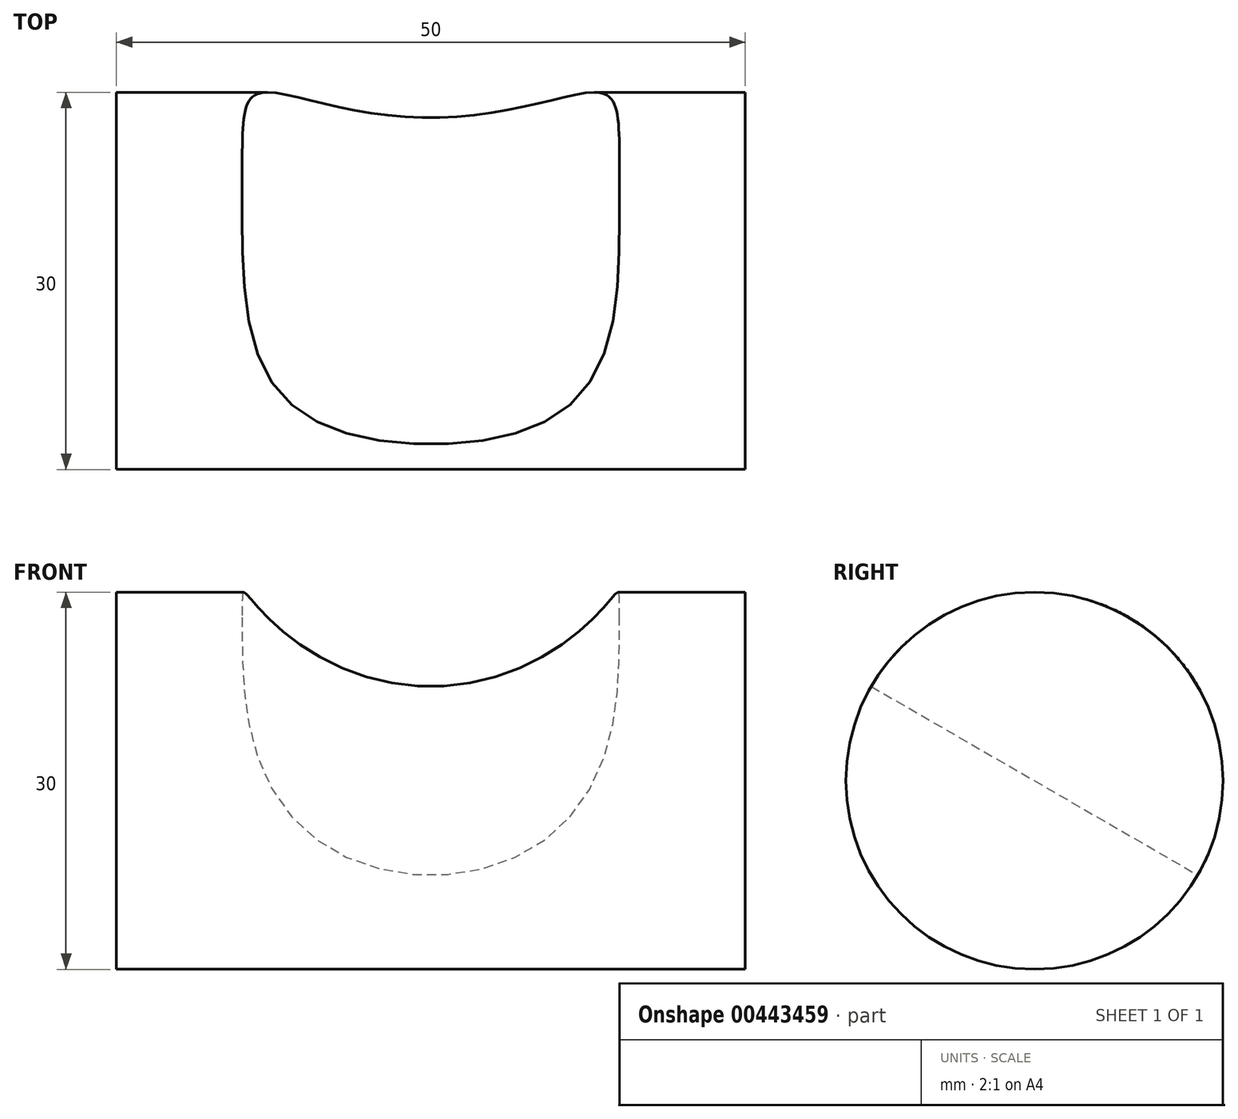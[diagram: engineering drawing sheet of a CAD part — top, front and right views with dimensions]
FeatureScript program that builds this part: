
annotation { "Feature Type Name" : "Feature", "Feature Type Description" : "" }
export const myFeature = defineFeature(function(context is Context, id is Id, definition is map)
    precondition{}
    {
        {
            var Q0;
            Q0=qCreatedBy(makeId("Right.planeOp"),FACE);
            var sketch = newSketch(context, id + "F0", { "sketchPlane" : qUnion([Q0])});
            skCircle(sketch, "E0", {"center": v(0, 0) * mm, "radius": 15 * mm});
            skSolve(sketch);
        }
        {
            var Q0;
            Q0=qSketchRegion(id+"F0",true);
            extrude(context, id + "F1", {"entities" : qUnion([Q0]), "depth" : 25 * mm, "hasSecondDirection" : true, "secondDirectionOppositeDirection" : true, "secondDirectionDepth" : 25 * mm});
        }
        {
            var Q0;
            Q0=qCreatedBy(makeId("Front.planeOp"),FACE);
            var sketch = newSketch(context, id + "F2", { "sketchPlane" : qUnion([Q0])});
            skCircle(sketch, "E1", {"center": v(0, -15) * mm, "radius": 15 * mm});
            skSolve(sketch);
        }
        {
            var Q0;
            Q0=qSketchRegion(id+"F2",true);
            extrude(context, id + "F3", {"entities" : qUnion([Q0]), "operationType" : NewBodyOperationType.REMOVE, "oppositeDirection" : true, "depth" : 25 * mm, "hasSecondDirection" : true, "secondDirectionOppositeDirection" : false, "secondDirectionDepth" : 25 * mm});
        }
        {
            var Q0;
            Q0=qCreatedBy(makeId("Top.planeOp"),FACE);
            var sketch = newSketch(context, id + "F4", { "sketchPlane" : qUnion([Q0])});
            skLineSegment(sketch, "E2", {"start": v(0, 0) * mm, "end": v(62.61, 0) * mm});
            skSolve(sketch);
        }
        {
            var Q0;
            Q0=makeQuery(id+"F1.opExtrude","SWEPT_BODY",BODY,{"disambiguationData":[OSD([sQuery(id+"F0.wireOp",EDGE,"E0")])]});
            var Q1;
            Q1=sQuery(id+"F4.wireOp",EDGE,"E2");
            transform(context, id + "F5", {"entities" : qUnion([Q0]), "transformType" : TransformType.ROTATION, "transformAxis" : qUnion([Q1]), "angle" : 180 * degree, "makeCopy" : false});
        }
        {
            var Q0;
            Q0=qCreatedBy(makeId("Top.planeOp"),FACE);
            var sketch = newSketch(context, id + "F6", { "sketchPlane" : qUnion([Q0])});
            skLineSegment(sketch, "E3", {"start": v(0, 0) * mm, "end": v(64.87, 0) * mm});
            skSolve(sketch);
        }
        {
            var Q0;
            Q0=makeQuery(id+"F1.opExtrude","SWEPT_BODY",BODY,{"disambiguationData":[OSD([sQuery(id+"F0.wireOp",EDGE,"E0")])]});
            var Q1;
            Q1=sQuery(id+"F6.wireOp",EDGE,"E3");
            transform(context, id + "F7", {"entities" : qUnion([Q0]), "transformType" : TransformType.ROTATION, "transformAxis" : qUnion([Q1]), "angle" : 330 * degree, "makeCopy" : false});
        }
    });
